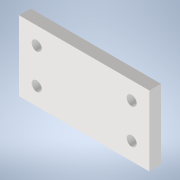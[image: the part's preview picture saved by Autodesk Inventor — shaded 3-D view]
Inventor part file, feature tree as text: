
AUTODESK INVENTOR PART (.ipt)
format: ipt  version: 2022 (Build 260153000, 153)  size: 104,448 bytes
history: native  units: mm
features: extrude x1, sketch x1
ambient origin geometry x8: Origin, YZ Plane, XZ Plane, XY Plane, X Axis, Y Axis, Z Axis, Center Point
bodies: Solid1 (feature_tree)
feature tree (2):
  extrude  "Extrusion1"  Depth=3.3mm
  sketch  "Sketch1"  dims[d24=9.95mm d27=9.95mm d31=5.0mm d32=5.0mm d33=5.0mm d34=5.0mm d35=3.3mm d36=0.0mm d40=5.0mm d41=5.0mm d42=5.0mm d43=27.0mm]
